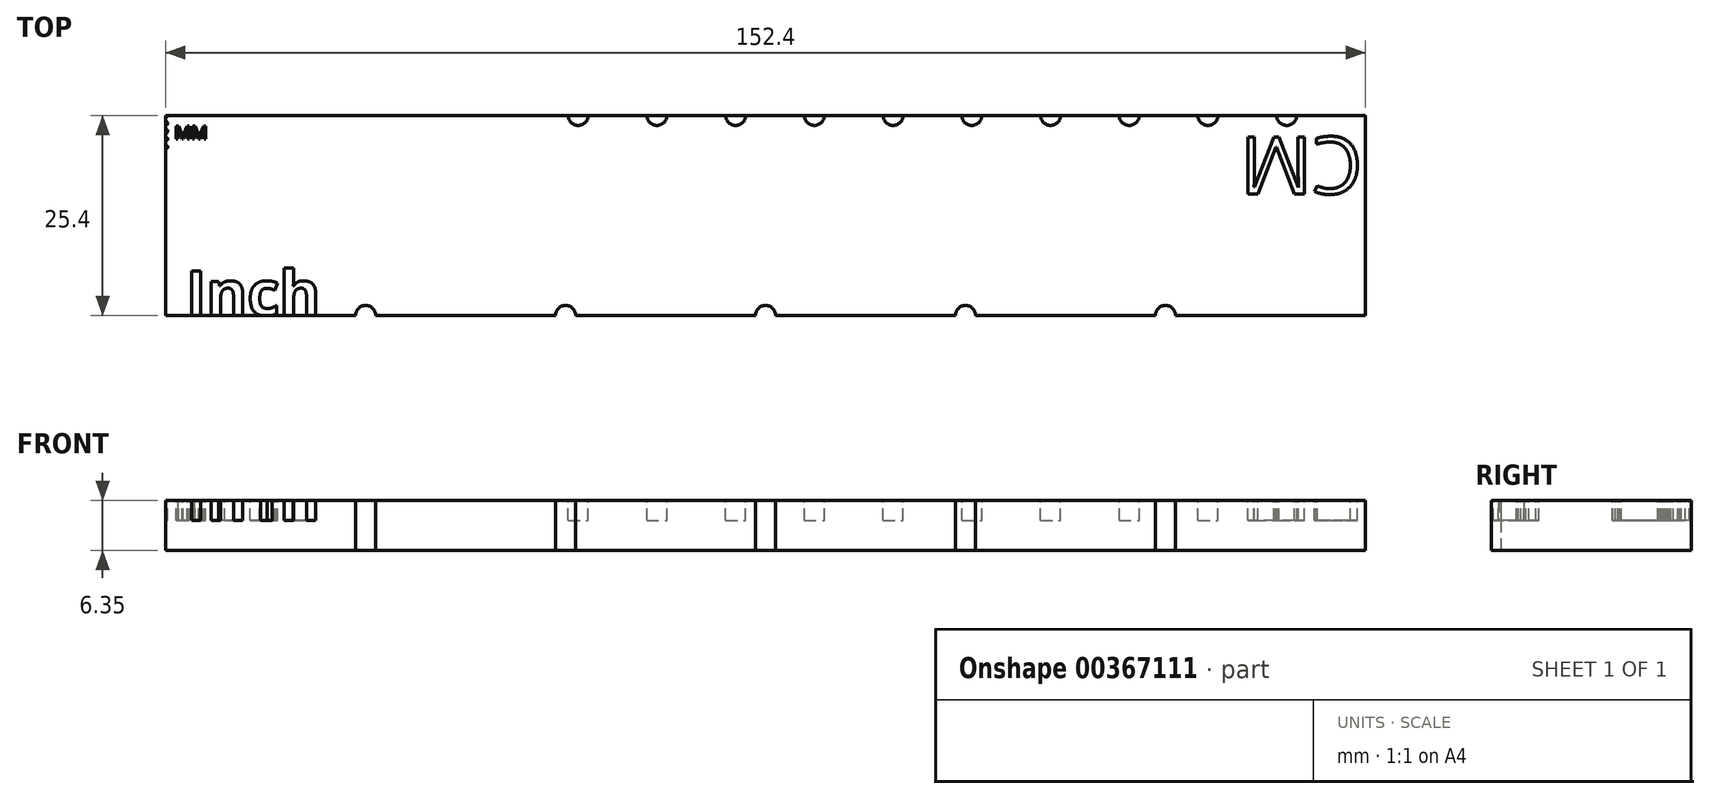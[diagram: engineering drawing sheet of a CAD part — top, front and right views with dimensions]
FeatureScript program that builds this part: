
annotation { "Feature Type Name" : "Feature", "Feature Type Description" : "" }
export const myFeature = defineFeature(function(context is Context, id is Id, definition is map)
    precondition{}
    {
        {
            var Q0;
            Q0=qCreatedBy(makeId("Top.planeOp"),FACE);
            var sketch = newSketch(context, id + "F0", { "sketchPlane" : qUnion([Q0])});
            skLineSegment(sketch, "E0.bottom", {"start": v(0, 0) * mm, "end": v(152.4, 0) * mm});
            skLineSegment(sketch, "E0.top", {"start": v(0, 25.4) * mm, "end": v(152.4, 25.4) * mm});
            skLineSegment(sketch, "E0.left", {"start": v(0, 0) * mm, "end": v(0, 25.4) * mm});
            skLineSegment(sketch, "E0.right", {"start": v(152.4, 0) * mm, "end": v(152.4, 25.4) * mm});
            skSolve(sketch);
        }
        {
            var Q0;
            Q0 = qSketchRegion(id + "F0", true);
            extrude(context, id + "F1", {"entities" : qUnion([Q0]), "depth" : 6.35 * mm});
        }
        {
            var Q0;
            Q0=makeQuery(id+"F1.opExtrude","CAP_FACE",FACE,{"disambiguationData":[OSD([sQuery(id+"F0.wireOp",EDGE,"E0.bottom"),sQuery(id+"F0.wireOp",EDGE,"E0.top"),sQuery(id+"F0.wireOp",EDGE,"E0.left"),sQuery(id+"F0.wireOp",EDGE,"E0.right")])],"isStart":false});
            var sketch = newSketch(context, id + "F2", { "sketchPlane" : qUnion([Q0])});
            skCircle(sketch, "E1", {"center": v(25.4, 0) * mm, "radius": 1.27 * mm});
            skCircle(sketch, "E2", {"center": v(50.8, 0) * mm, "radius": 1.27 * mm});
            skCircle(sketch, "E3", {"center": v(76.2, 0) * mm, "radius": 1.27 * mm});
            skCircle(sketch, "E4", {"center": v(101.6, 0) * mm, "radius": 1.27 * mm});
            skCircle(sketch, "E5", {"center": v(127, 0) * mm, "radius": 1.27 * mm});
            skSolve(sketch);
        }
        {
            var Q0;
            Q0 = qSketchRegion(id + "F2", true);
            extrude(context, id + "F3", {"entities" : qUnion([Q0]), "operationType" : NewBodyOperationType.REMOVE, "oppositeDirection" : true, "depth" : 25.4 * mm});
        }
        {
            var Q0;
            Q0=makeQuery(id+"F1.opExtrude","CAP_FACE",FACE,{"disambiguationData":[OSD([sQuery(id+"F0.wireOp",EDGE,"E0.bottom"),sQuery(id+"F0.wireOp",EDGE,"E0.top"),sQuery(id+"F0.wireOp",EDGE,"E0.left"),sQuery(id+"F0.wireOp",EDGE,"E0.right")])],"isStart":false});
            var sketch = newSketch(context, id + "F4", { "sketchPlane" : qUnion([Q0])});
            skText(sketch, "E6", { "text": "Inch", "fontName": "OpenSans-Bold.ttf"});
            const initialGuessF4  = {"E6": [0.00256, 0, 1, 0, 0.0057]};
            skSetInitialGuess(sketch, initialGuessF4);
            skSolve(sketch);
        }
        {
            var Q0;
            Q0 = qSketchRegion(id + "F4", true);
            extrude(context, id + "F5", {"entities" : qUnion([Q0]), "operationType" : NewBodyOperationType.REMOVE, "oppositeDirection" : true, "depth" : 2.54 * mm});
        }
        {
            var Q0;
            {var subQ0=sQuery(id+"F0.wireOp",EDGE,"E0.right");var subQ1=sQuery(id+"F0.wireOp",EDGE,"E0.left");var subQ2=sQuery(id+"F0.wireOp",EDGE,"E0.top");var subQ3=sQuery(id+"F0.wireOp",EDGE,"E0.bottom");Q0=makeQuery(id+"F5.boolean.opBoolean","SPLIT",FACE,{"disambiguationData":[TD([makeQuery(id+"F1.opExtrude","SWEPT_FACE",FACE,{"disambiguationData":[OSD([subQ2])]})])],"derivedFrom":makeQuery(id+"F1.opExtrude","CAP_FACE",FACE,{"disambiguationData":[OSD([subQ3,subQ2,subQ1,subQ0])],"isStart":false})});}
            var sketch = newSketch(context, id + "F6", { "sketchPlane" : qUnion([Q0])});
            skText(sketch, "E7", { "text": "CM", "fontName": "OpenSans-Regular.ttf"});
            const initialGuessF6  = {"E7": [0.152, 0.02267, -1, 0, 0.00728]};
            skSetInitialGuess(sketch, initialGuessF6);
            skSolve(sketch);
        }
        {
            var Q0;
            Q0 = qSketchRegion(id + "F6", true);
            extrude(context, id + "F7", {"entities" : qUnion([Q0]), "operationType" : NewBodyOperationType.REMOVE, "oppositeDirection" : true, "depth" : 2.54 * mm});
        }
        {
            var Q0;
            {var subQ0=sQuery(id+"F0.wireOp",EDGE,"E0.right");var subQ1=sQuery(id+"F0.wireOp",EDGE,"E0.left");var subQ2=sQuery(id+"F0.wireOp",EDGE,"E0.top");var subQ3=sQuery(id+"F0.wireOp",EDGE,"E0.bottom");Q0=makeQuery(id+"F5.boolean.opBoolean","SPLIT",FACE,{"disambiguationData":[TD([makeQuery(id+"F1.opExtrude","SWEPT_FACE",FACE,{"disambiguationData":[OSD([subQ2])]})])],"derivedFrom":makeQuery(id+"F1.opExtrude","CAP_FACE",FACE,{"disambiguationData":[OSD([subQ3,subQ2,subQ1,subQ0])],"isStart":false})});}
            var sketch = newSketch(context, id + "F8", { "sketchPlane" : qUnion([Q0])});
            skCircle(sketch, "E8", {"center": v(142.4, 25.4) * mm, "radius": 1.27 * mm});
            skCircle(sketch, "E9", {"center": v(132.4, 25.4) * mm, "radius": 1.27 * mm});
            skCircle(sketch, "E10", {"center": v(122.4, 25.4) * mm, "radius": 1.27 * mm});
            skCircle(sketch, "E11", {"center": v(112.4, 25.4) * mm, "radius": 1.27 * mm});
            skCircle(sketch, "E12", {"center": v(52.4, 25.4) * mm, "radius": 1.27 * mm});
            skCircle(sketch, "E13", {"center": v(102.4, 25.4) * mm, "radius": 1.27 * mm});
            skCircle(sketch, "E14", {"center": v(92.4, 25.4) * mm, "radius": 1.27 * mm});
            skCircle(sketch, "E15", {"center": v(82.4, 25.4) * mm, "radius": 1.27 * mm});
            skCircle(sketch, "E16", {"center": v(72.4, 25.4) * mm, "radius": 1.27 * mm});
            skCircle(sketch, "E17", {"center": v(62.4, 25.4) * mm, "radius": 1.27 * mm});
            skSolve(sketch);
        }
        {
            var Q0;
            Q0 = qSketchRegion(id + "F8", true);
            extrude(context, id + "F9", {"entities" : qUnion([Q0]), "operationType" : NewBodyOperationType.REMOVE, "oppositeDirection" : true, "depth" : 2.54 * mm});
        }
        {
            var Q0;
            {var subQ0=sQuery(id+"F0.wireOp",EDGE,"E0.right");var subQ1=sQuery(id+"F0.wireOp",EDGE,"E0.left");var subQ2=sQuery(id+"F0.wireOp",EDGE,"E0.top");var subQ3=sQuery(id+"F0.wireOp",EDGE,"E0.bottom");Q0=makeQuery(id+"F5.boolean.opBoolean","SPLIT",FACE,{"disambiguationData":[TD([makeQuery(id+"F1.opExtrude","SWEPT_FACE",FACE,{"disambiguationData":[OSD([subQ2])]})])],"derivedFrom":makeQuery(id+"F1.opExtrude","CAP_FACE",FACE,{"disambiguationData":[OSD([subQ3,subQ2,subQ1,subQ0])],"isStart":false})});}
            var sketch = newSketch(context, id + "F10", { "sketchPlane" : qUnion([Q0])});
            skCircle(sketch, "E18", {"center": v(0, 25.4) * mm, "radius": 0.25 * mm});
            skCircle(sketch, "E19", {"center": v(0, 24.4) * mm, "radius": 0.25 * mm});
            skCircle(sketch, "E20", {"center": v(0, 23.4) * mm, "radius": 0.25 * mm});
            skCircle(sketch, "E21", {"center": v(0, 22.4) * mm, "radius": 0.25 * mm});
            skCircle(sketch, "E22", {"center": v(0, 21.4) * mm, "radius": 0.25 * mm});
            skSolve(sketch);
        }
        {
            var Q0;
            Q0 = qSketchRegion(id + "F10", true);
            extrude(context, id + "F11", {"entities" : qUnion([Q0]), "operationType" : NewBodyOperationType.REMOVE, "oppositeDirection" : true, "depth" : 2.54 * mm});
        }
        {
            var Q0;
            {var subQ0=sQuery(id+"F0.wireOp",EDGE,"E0.right");var subQ1=sQuery(id+"F0.wireOp",EDGE,"E0.left");var subQ2=sQuery(id+"F0.wireOp",EDGE,"E0.top");var subQ3=sQuery(id+"F0.wireOp",EDGE,"E0.bottom");Q0=makeQuery(id+"F5.boolean.opBoolean","SPLIT",FACE,{"disambiguationData":[TD([makeQuery(id+"F1.opExtrude","SWEPT_FACE",FACE,{"disambiguationData":[OSD([subQ2])]})])],"derivedFrom":makeQuery(id+"F1.opExtrude","CAP_FACE",FACE,{"disambiguationData":[OSD([subQ3,subQ2,subQ1,subQ0])],"isStart":false})});}
            var sketch = newSketch(context, id + "F12", { "sketchPlane" : qUnion([Q0])});
            skText(sketch, "E23", { "text": "MM", "fontName": "OpenSans-Regular.ttf"});
            const initialGuessF12  = {"E23": [0.0011, 0.0224, 1, 0, 0.00169]};
            skSetInitialGuess(sketch, initialGuessF12);
            skSolve(sketch);
        }
        {
            var Q0;
            Q0 = qSketchRegion(id + "F12", true);
            extrude(context, id + "F13", {"entities" : qUnion([Q0]), "operationType" : NewBodyOperationType.REMOVE, "oppositeDirection" : true, "depth" : 2.54 * mm});
        }
    });
